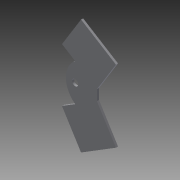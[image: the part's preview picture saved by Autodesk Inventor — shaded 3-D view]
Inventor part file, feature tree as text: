
AUTODESK INVENTOR PART (.ipt)
format: ipt  version: 2015 (Build 190159000, 159)  size: 91,136 bytes
history: native  units: mm
features: extrude x1, sketch x1
ambient origin geometry x8: Origin, YZ Plane, XZ Plane, XY Plane, X Axis, Y Axis, Z Axis, Center Point
bodies: Solid1 (feature_tree)
feature tree (2):
  extrude  "Extrusion1"  Depth=35.0mm
  sketch  "Sketch1"  dims[d5=10.0mm d6=35.0mm d7=35.0mm d8=35.0mm d9=35.0mm d10=36.0mm d12=6.0mm d13=15.0mm d14=15.0mm d15=2.0mm d16=0.0mm]
